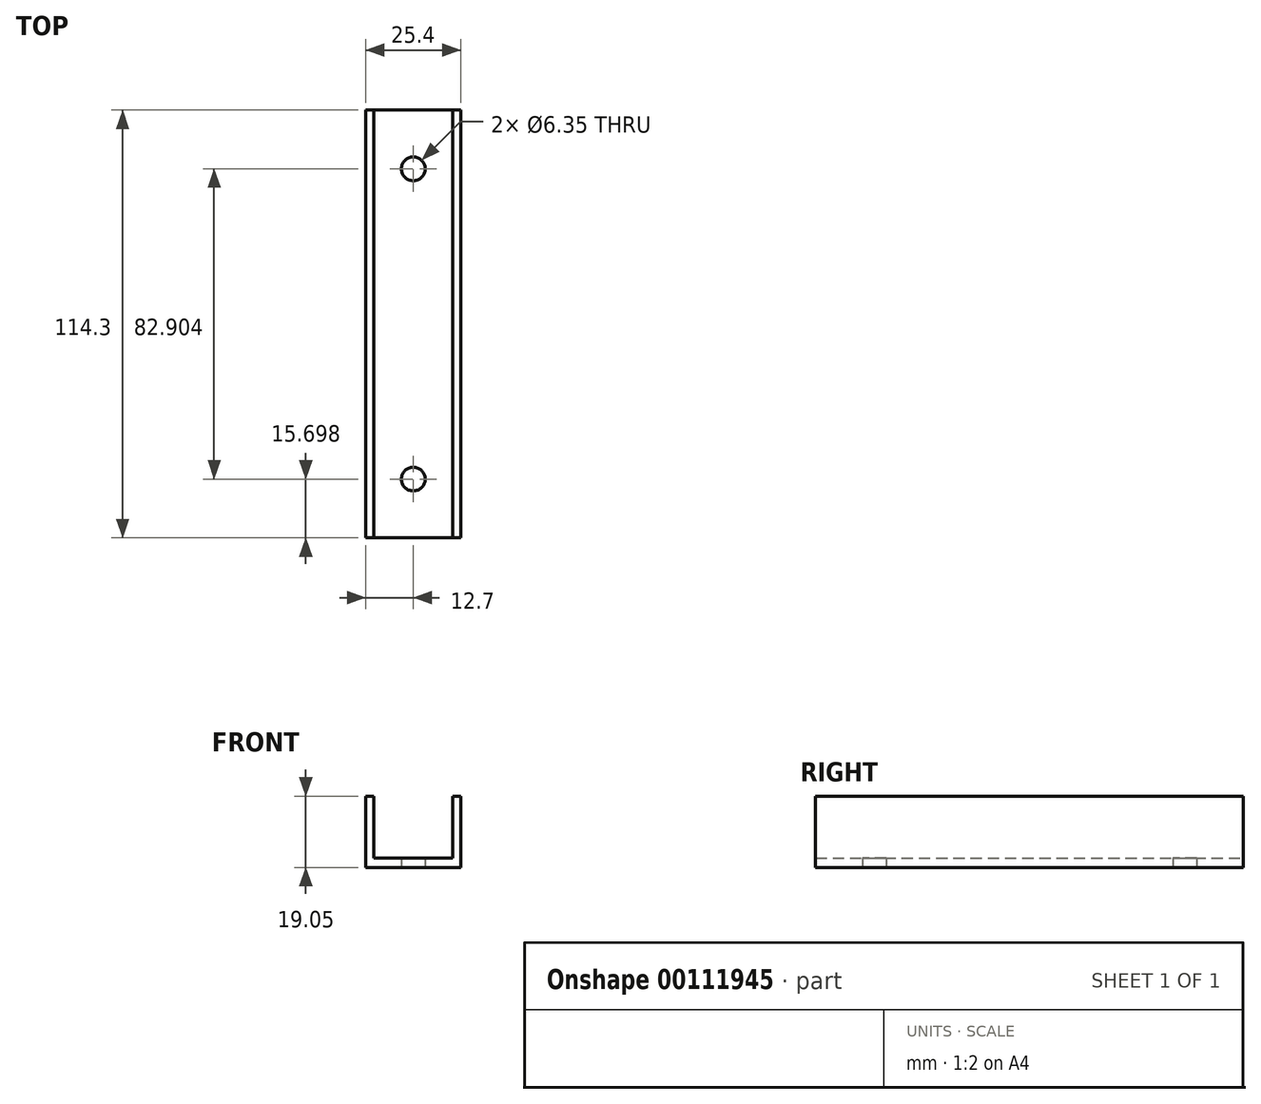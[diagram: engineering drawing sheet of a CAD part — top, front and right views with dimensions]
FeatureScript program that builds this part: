
annotation { "Feature Type Name" : "Feature", "Feature Type Description" : "" }
export const myFeature = defineFeature(function(context is Context, id is Id, definition is map)
    precondition{}
    {
        {
            var Q0;
            Q0=qCreatedBy(makeId("Top.planeOp"),FACE);
            var sketch = newSketch(context, id + "F0", { "sketchPlane" : qUnion([Q0])});
            skLineSegment(sketch, "E0.bottom", {"start": v(12.7, -57.15) * mm, "end": v(-12.7, -57.15) * mm});
            skLineSegment(sketch, "E0.top", {"start": v(12.7, 57.15) * mm, "end": v(-12.7, 57.15) * mm});
            skLineSegment(sketch, "E0.left", {"start": v(12.7, -57.15) * mm, "end": v(12.7, 57.15) * mm});
            skLineSegment(sketch, "E0.right", {"start": v(-12.7, -57.15) * mm, "end": v(-12.7, 57.15) * mm});
            skPoint(sketch, "E0.middle", {"position": v(0, 0) * mm});
            skCircle(sketch, "E1", {"center": v(0, 41.45) * mm, "radius": 3.18 * mm});
            skCircle(sketch, "E2.MirrorC", {"center": v(0, -41.45) * mm, "radius": 3.18 * mm});
            skLineSegment(sketch, "E3", {"start": v(0, 41.45) * mm, "end": v(0, 57.15) * mm});
            skSolve(sketch);
        }
        {
            var Q0;
            Q0 = qSketchRegion(id + "F0", true);
            extrude(context, id + "F1", {"entities" : qUnion([Q0]), "depth" : 19.05 * mm});
        }
        {
            var Q0;
            Q0=makeQuery(id+"F1.opExtrude","SWEPT_FACE",FACE,{"disambiguationData":[OSD([sQuery(id+"F0.wireOp",EDGE,"E0.top")])]});
            var sketch = newSketch(context, id + "F2", { "sketchPlane" : qUnion([Q0])});
            skLineSegment(sketch, "E4.bottom", {"start": v(10.57, 2.51) * mm, "end": v(-10.57, 2.51) * mm});
            skLineSegment(sketch, "E4.top", {"start": v(10.57, 25.66) * mm, "end": v(-10.57, 25.66) * mm});
            skLineSegment(sketch, "E4.left", {"start": v(10.57, 2.51) * mm, "end": v(10.57, 25.66) * mm});
            skLineSegment(sketch, "E4.right", {"start": v(-10.57, 2.51) * mm, "end": v(-10.57, 25.66) * mm});
            skPoint(sketch, "E4.middle", {"position": v(0, 14.09) * mm});
            skSolve(sketch);
        }
        {
            var Q0;
            Q0 = qSketchRegion(id + "F2", true);
            extrude(context, id + "F3", {"entities" : qUnion([Q0]), "operationType" : NewBodyOperationType.REMOVE, "oppositeDirection" : true, "depth" : 140.54 * mm});
        }
    });
